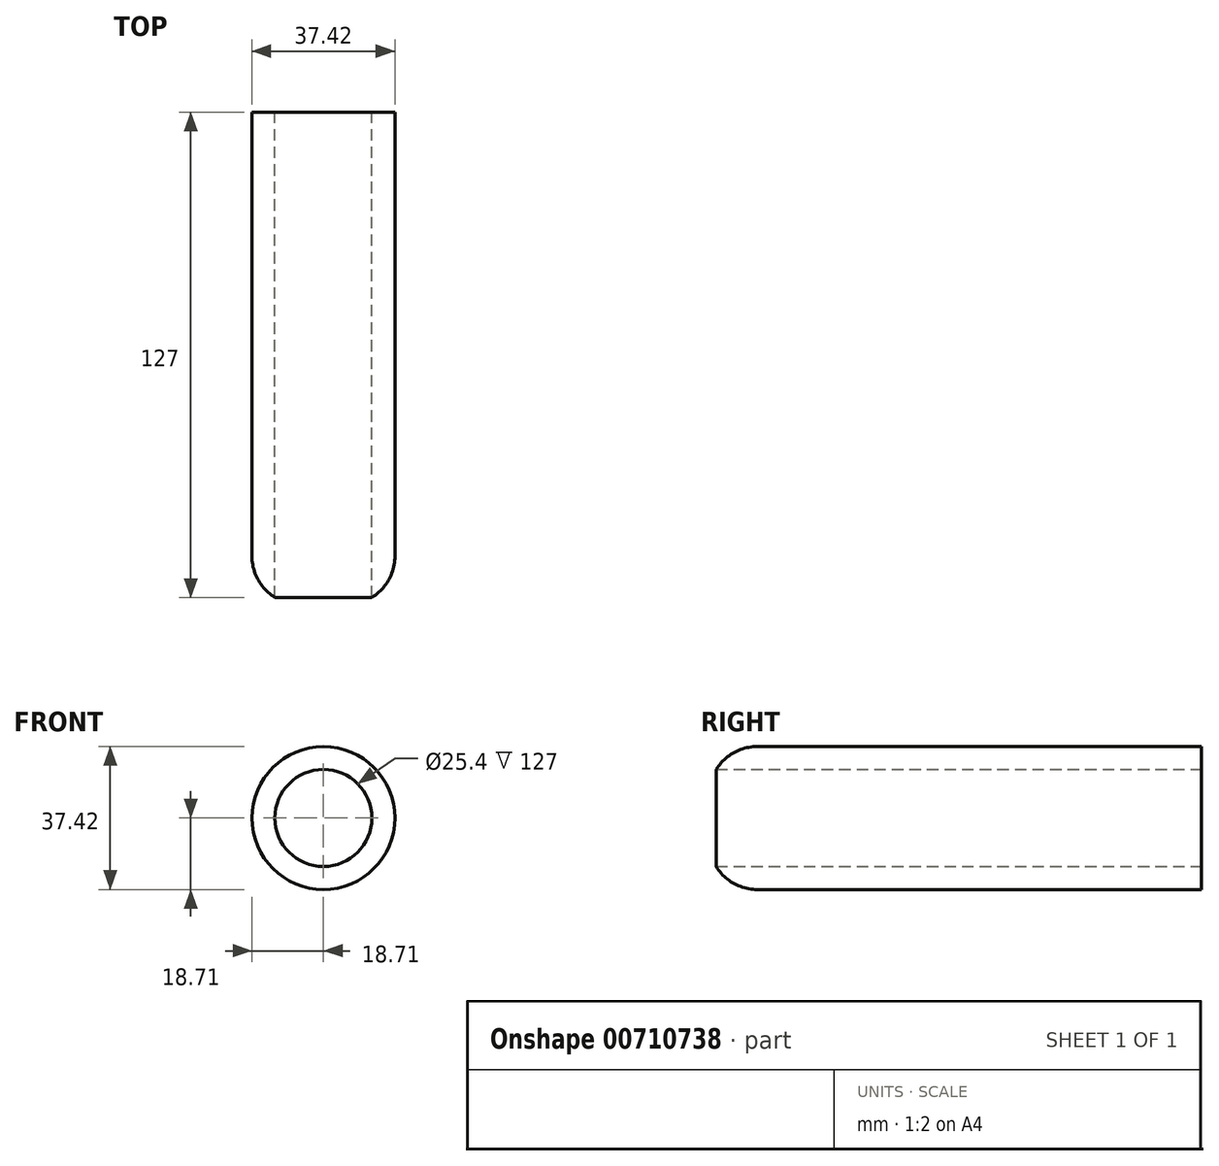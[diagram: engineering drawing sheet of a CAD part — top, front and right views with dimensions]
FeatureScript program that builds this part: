
annotation { "Feature Type Name" : "Feature", "Feature Type Description" : "" }
export const myFeature = defineFeature(function(context is Context, id is Id, definition is map)
    precondition{}
    {
        {
            var Q0;
            Q0=qCreatedBy(makeId("Front.planeOp"),FACE);
            var sketch = newSketch(context, id + "F0", { "sketchPlane" : qUnion([Q0])});
            skCircle(sketch, "E0", {"center": v(0, 0) * mm, "radius": 18.7 * mm});
            skSolve(sketch);
        }
        {
            var Q0;
            Q0=makeQuery(id+"F0.imprint","IMPRINT",FACE,{"disambiguationData":[TD([[makeQuery(id+"F0.imprint","IMPRINT",EDGE,{"derivedFrom":sQuery(id+"F0.wireOp",EDGE,"E0")}),1.0]])]});
            extrude(context, id + "F1", {"entities" : qUnion([Q0]), "oppositeDirection" : true, "depth" : 127 * mm, "offsetDistance" : 25.4 * mm});
        }
        {
            var Q0;
            Q0=qCreatedBy(makeId("Front.planeOp"),FACE);
            var sketch = newSketch(context, id + "F2", { "sketchPlane" : qUnion([Q0])});
            skCircle(sketch, "E1", {"center": v(0, 0) * mm, "radius": 11.65 * mm});
            skSolve(sketch);
        }
        {
            var Q0;
            Q0=sQuery(id+"F2.wireOp",VERTEX,"E1.center");
            var Q1;
            Q1=makeQuery(id+"F1.opExtrude","SWEPT_BODY",BODY,{"disambiguationData":[OSD([sQuery(id+"F0.wireOp",EDGE,"E0")])]});
            hole(context, id + "F3", {"style" : HoleStyle.SIMPLE, "endStyle" : HoleEndStyle.THROUGH, "holeDiameter" : 25.4 * mm, "majorDiameter" : 6.35 * mm, "isTappedThrough" : true, "tappedDepth" : 12.7 * mm, "tapClearance" : 3, "startFromSketch" : true, "locations" : qUnion([Q0]), "scope" : qUnion([Q1])});
        }
        {
            var Q0;
            Q0=makeQuery(id+"F1.opExtrude","CAP_EDGE",EDGE,{"disambiguationData":[OSD([sQuery(id+"F0.wireOp",EDGE,"E0")])],"isStart":true});
            fillet(context, id + "F4", {"entities" : qUnion([Q0]), "radius" : 12.7 * mm, "tangentPropagation" : true, "allowEdgeOverflow" : false});
        }
    });
